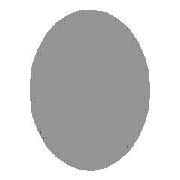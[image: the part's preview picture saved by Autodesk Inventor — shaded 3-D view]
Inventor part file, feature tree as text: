
AUTODESK INVENTOR PART (.ipt)
format: ipt  version: 2013 (Build 170138000, 138)  size: 117,760 bytes
history: native  units: mm (DEFAULTED — no unit token found)
features: plane x7, sketch x5, other x4, extrude x2
ambient origin geometry x8: Origin, YZ Plane, XZ Plane, XY Plane, X Axis, Y Axis, Z Axis, Center Point
bodies: Solid1 (feature_tree), Body (feature_tree)
feature tree (18):
  parser-record x1  (decoder bookkeeping rows leaked as tree rows — omitted from the tree; the rows remain in map.json)
  other  "Driven Length"
  other  "Start plane"
  other  "End plane"
  plane  "Work Plane4"
  plane  "Work Plane5"
  plane  "Work Plane6"
  extrude  "Extrusion2"  Depth=641.35mm
  plane  "Work Plane7"
  plane  "Work Plane8"
  plane  "Work Plane9"
  extrude  "Extrusion3"  TaperAngle=0.0deg  [1 undecoded]
  sketch  "Sketch"  dims[d7=641.35mm d8=3.302mm d9=0.0mm d10=3.302mm d11=0.0mm]
  sketch  "Sketch2"  dims[d0=38.1mm d1=641.35mm]
  plane  "Work Plane3"
  sketch  "Sketch3"  dims[d2=0.0mm d4=-0.0mm]
  sketch  "Sketch4"  dims[d5=641.35mm]
  sketch  "Sketch5"  dims[d6=90.0deg]
note: 1 required parameter value undecoded (feature->parameter linkage not recoverable at this tier; creation-order binding heuristic only, values carry confidence <= 0.55)
